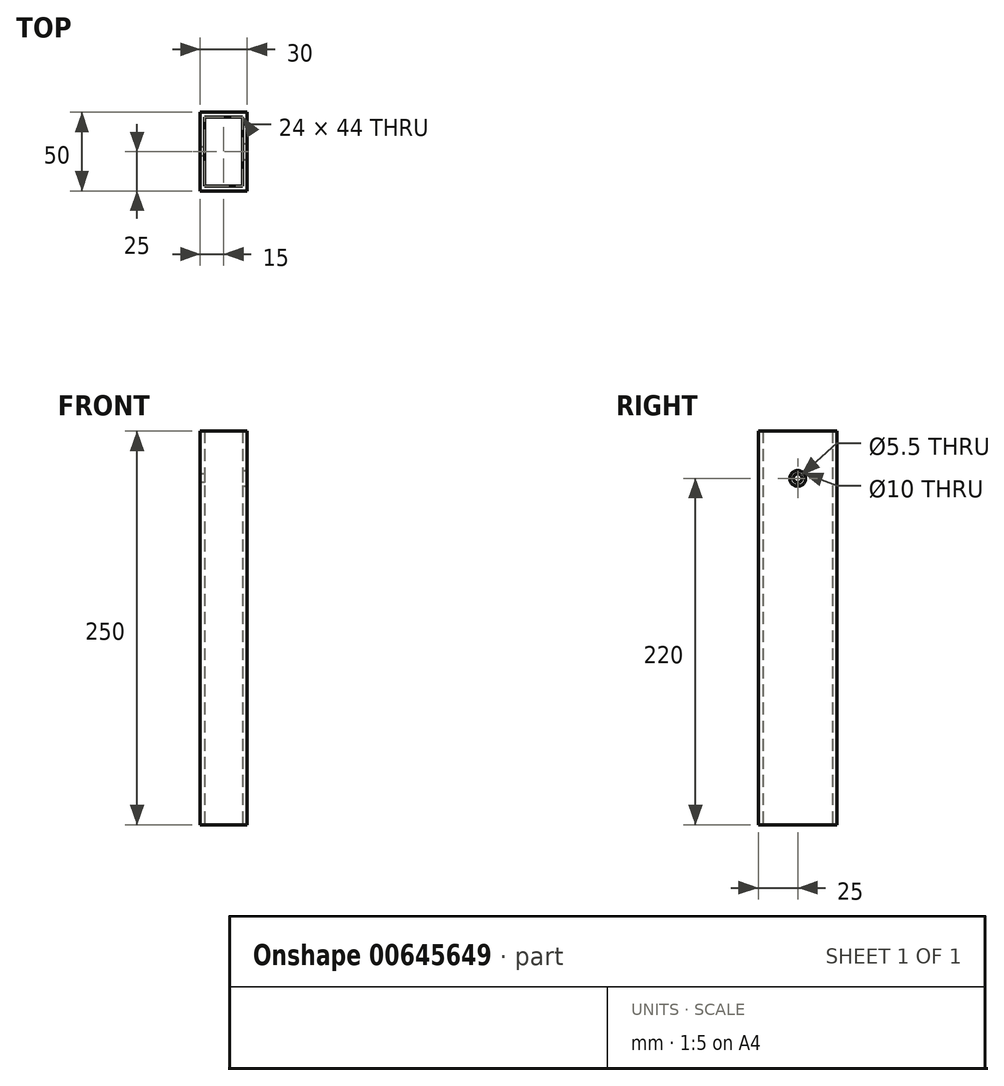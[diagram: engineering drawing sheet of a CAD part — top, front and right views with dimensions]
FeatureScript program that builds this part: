
annotation { "Feature Type Name" : "Feature", "Feature Type Description" : "" }
export const myFeature = defineFeature(function(context is Context, id is Id, definition is map)
    precondition{}
    {
        {
            var Q0;
            Q0=qCreatedBy(makeId("Top.planeOp"),FACE);
            var sketch = newSketch(context, id + "F0", { "sketchPlane" : qUnion([Q0])});
            skLineSegment(sketch, "E0.bottom", {"start": v(0, 0) * mm, "end": v(30, 0) * mm});
            skLineSegment(sketch, "E0.top", {"start": v(0, 50) * mm, "end": v(30, 50) * mm});
            skLineSegment(sketch, "E0.left", {"start": v(0, 0) * mm, "end": v(0, 50) * mm});
            skLineSegment(sketch, "E0.right", {"start": v(30, 0) * mm, "end": v(30, 50) * mm});
            skLineSegment(sketch, "E1.0", {"start": v(3, 3) * mm, "end": v(3, 47) * mm});
            skLineSegment(sketch, "E1.1", {"start": v(3, 3) * mm, "end": v(27, 3) * mm});
            skLineSegment(sketch, "E1.2", {"start": v(27, 3) * mm, "end": v(27, 47) * mm});
            skLineSegment(sketch, "E1.3", {"start": v(3, 47) * mm, "end": v(27, 47) * mm});
            skSolve(sketch);
        }
        {
            var Q0;
            Q0=makeQuery(id+"F0.imprint","IMPRINT",FACE,{"disambiguationData":[TD([[makeQuery(id+"F0.imprint","IMPRINT",EDGE,{"derivedFrom":sQuery(id+"F0.wireOp",EDGE,"E0.bottom")}),1.0]])]});
            extrude(context, id + "F1", {"entities" : qUnion([Q0]), "depth" : 250 * mm, "offsetDistance" : 25 * mm});
        }
        {
            var Q0;
            Q0=makeQuery(id+"F1.opExtrude","SWEPT_FACE",FACE,{"disambiguationData":[OSD([sQuery(id+"F0.wireOp",EDGE,"E0.left")])]});
            var sketch = newSketch(context, id + "F2", { "sketchPlane" : qUnion([Q0])});
            skPoint(sketch, "E2", {"position": v(-25, 220) * mm});
            skSolve(sketch);
        }
        {
            var Q0;
            Q0=sQuery(id+"F2.wireOp",VERTEX,"E2");
            var Q1;
            Q1=makeQuery(id+"F1.opExtrude","SWEPT_BODY",BODY,{"disambiguationData":[OSD([sQuery(id+"F0.wireOp",EDGE,"E0.bottom"),sQuery(id+"F0.wireOp",EDGE,"E0.top"),sQuery(id+"F0.wireOp",EDGE,"E0.left"),sQuery(id+"F0.wireOp",EDGE,"E0.right"),sQuery(id+"F0.wireOp",EDGE,"E1.0"),sQuery(id+"F0.wireOp",EDGE,"E1.1"),sQuery(id+"F0.wireOp",EDGE,"E1.2"),sQuery(id+"F0.wireOp",EDGE,"E1.3")])]});
            hole(context, id + "F3", {"style" : HoleStyle.SIMPLE, "endStyle" : HoleEndStyle.THROUGH, "holeDiameter" : 5.5 * mm, "majorDiameter" : 5 * mm, "isTappedThrough" : true, "tappedDepth" : 12 * mm, "tapClearance" : 3, "locations" : qUnion([Q0]), "scope" : qUnion([Q1])});
        }
        {
            var Q0;
            Q0=makeQuery(id+"F1.opExtrude","SWEPT_FACE",FACE,{"disambiguationData":[OSD([sQuery(id+"F0.wireOp",EDGE,"E0.right")])]});
            var sketch = newSketch(context, id + "F4", { "sketchPlane" : qUnion([Q0])});
            skPoint(sketch, "E3", {"position": v(25, 220) * mm});
            skSolve(sketch);
        }
        {
            var Q0;
            Q0=sQuery(id+"F4.wireOp",VERTEX,"E3");
            var Q1;
            Q1=makeQuery(id+"F1.opExtrude","SWEPT_BODY",BODY,{"disambiguationData":[OSD([sQuery(id+"F0.wireOp",EDGE,"E0.bottom"),sQuery(id+"F0.wireOp",EDGE,"E0.top"),sQuery(id+"F0.wireOp",EDGE,"E0.left"),sQuery(id+"F0.wireOp",EDGE,"E0.right"),sQuery(id+"F0.wireOp",EDGE,"E1.0"),sQuery(id+"F0.wireOp",EDGE,"E1.1"),sQuery(id+"F0.wireOp",EDGE,"E1.2"),sQuery(id+"F0.wireOp",EDGE,"E1.3")])]});
            hole(context, id + "F5", {"style" : HoleStyle.SIMPLE, "endStyle" : HoleEndStyle.BLIND, "holeDiameter" : 10 * mm, "majorDiameter" : 5 * mm, "holeDepth" : 5 * mm, "isTappedThrough" : true, "tappedDepth" : 12 * mm, "tapClearance" : 3, "locations" : qUnion([Q0]), "scope" : qUnion([Q1])});
        }
    });
